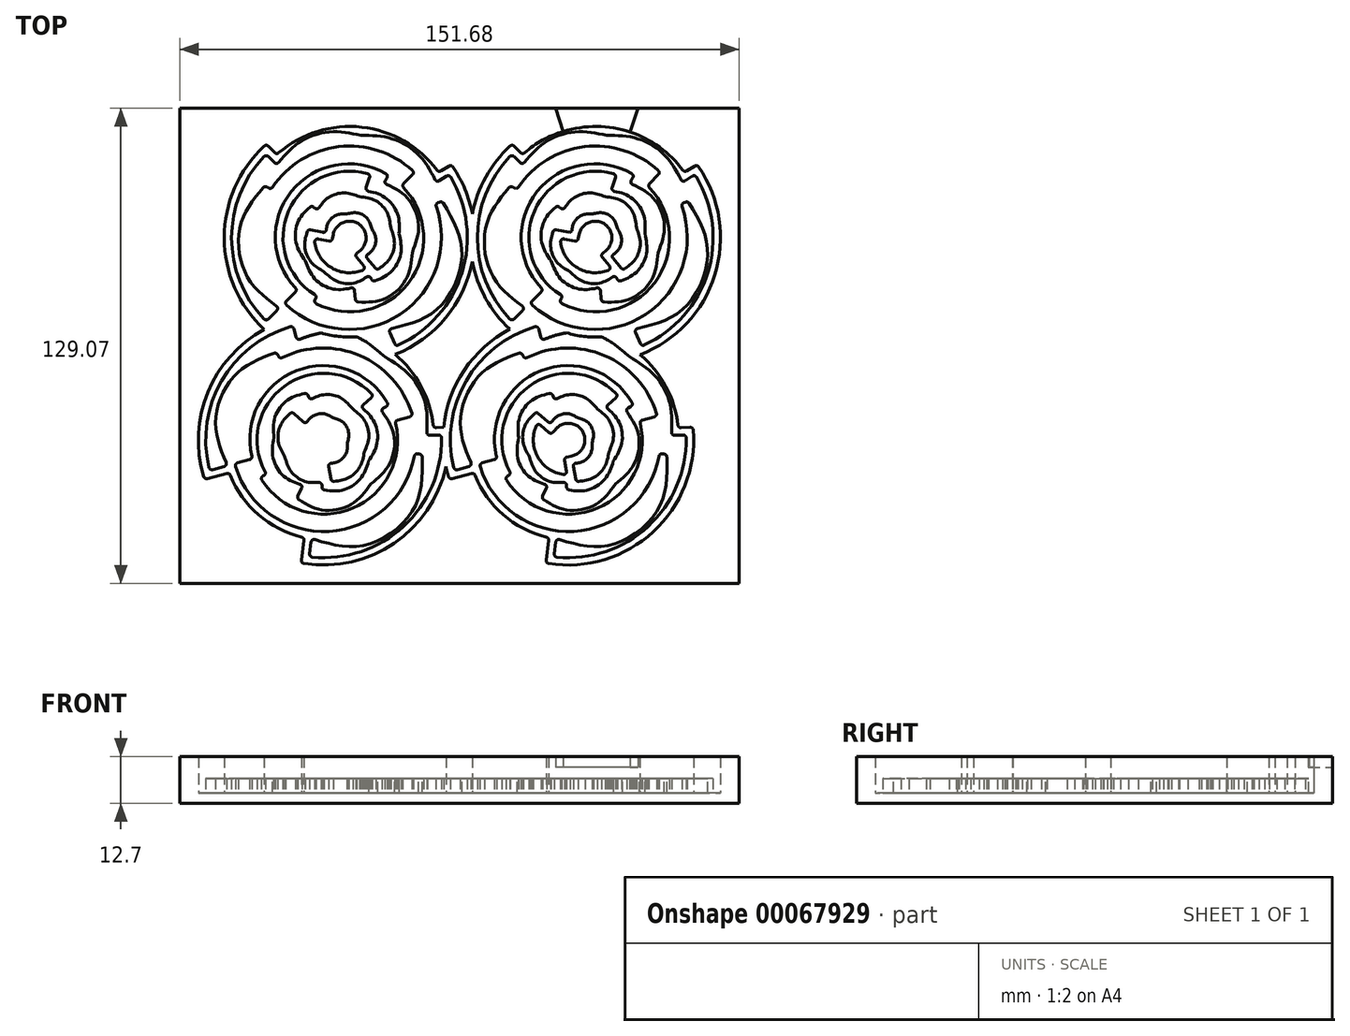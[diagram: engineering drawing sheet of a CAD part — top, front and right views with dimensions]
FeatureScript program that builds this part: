
annotation { "Feature Type Name" : "Feature", "Feature Type Description" : "" }
export const myFeature = defineFeature(function(context is Context, id is Id, definition is map)
    precondition{}
    {
        {
            var Q0;
            Q0=qCreatedBy(makeId("Front.planeOp"),FACE);
            var sketch = newSketch(context, id + "F0", { "sketchPlane" : qUnion([Q0])});
            skCircle(sketch, "E0", {"center": v(0, -1.15) * mm, "radius": 34.66 * mm});
            skSolve(sketch);
        }
        {
            var Q0;
            Q0 = qSketchRegion(id + "F0", true);
            extrude(context, id + "F1", {"entities" : qUnion([Q0]), "depth" : 4 * mm});
        }
        {
            var Q0;
            Q0=qCreatedBy(makeId("Front.planeOp"),FACE);
            var sketch = newSketch(context, id + "F2", { "sketchPlane" : qUnion([Q0])});
            skLineSegment(sketch, "E1", {"start": v(14.14, -15.15) * mm, "end": v(17.68, -18.69) * mm});
            skLineSegment(sketch, "E2", {"start": v(-21.29, -14.11) * mm, "end": v(-23, -15.16) * mm});
            skFitSpline(sketch, "E3", {"points": [v(-23, -15.16) * mm, v(-29.55, -4.51) * mm, v(-27.93, 9.24) * mm, v(-19.1, 18.08) * mm]});
            skLineSegment(sketch, "E4", {"start": v(-19.1, 18.08) * mm, "end": v(-22.63, 21.62) * mm});
            skLineSegment(sketch, "E5", {"start": v(-22.63, -23.64) * mm, "end": v(-19.8, -20.8) * mm});
            skFitSpline(sketch, "E6", {"points": [v(3.07, -28.84) * mm, v(-5.38, -29.77) * mm, v(-13.8, -26.82) * mm, v(-19.8, -20.8) * mm]});
            skFitSpline(sketch, "E7", {"points": [v(23.63, -16.03) * mm, v(19.08, -23.2) * mm, v(11.51, -27.91) * mm, v(3.07, -28.84) * mm]});
            skLineSegment(sketch, "E8", {"start": v(23.63, -16.03) * mm, "end": v(27.01, -18.17) * mm});
            skLineSegment(sketch, "E9", {"start": v(12.52, 28.44) * mm, "end": v(10.56, 23.84) * mm});
            skFitSpline(sketch, "E10", {"points": [v(10.56, 23.84) * mm, v(24.04, 18.11) * mm, v(30.5, 2.69) * mm, v(25.11, -10.93) * mm]});
            skLineSegment(sketch, "E11", {"start": v(25.11, -10.93) * mm, "end": v(23.25, -10.2) * mm});
            skLineSegment(sketch, "E12", {"start": v(-17.68, 16.67) * mm, "end": v(-14.14, 13.13) * mm});
            skLineSegment(sketch, "E13", {"start": v(10.59, -17.98) * mm, "end": v(9.26, -15.86) * mm});
            skFitSpline(sketch, "E14", {"points": [v(17.04, 3) * mm, v(18.75, -4.3) * mm, v(15.63, -11.89) * mm, v(9.26, -15.86) * mm]});
            skFitSpline(sketch, "E15", {"points": [v(1.68, 16.4) * mm, v(9.15, 15.69) * mm, v(15.32, 10.3) * mm, v(17.04, 3) * mm]});
            skLineSegment(sketch, "E16", {"start": v(1.68, 16.4) * mm, "end": v(1.3, 12.43) * mm});
            skFitSpline(sketch, "E17", {"points": [v(-11.98, 5.22) * mm, v(-9.44, 10.1) * mm, v(-4.18, 12.96) * mm, v(1.3, 12.43) * mm]});
            skFitSpline(sketch, "E18", {"points": [v(-10.25, -9.79) * mm, v(-13.84, -5.6) * mm, v(-14.52, 0.33) * mm, v(-11.98, 5.22) * mm]});
            skLineSegment(sketch, "E19", {"start": v(-10.25, -9.79) * mm, "end": v(-8.74, -8.49) * mm});
            skFitSpline(sketch, "E20", {"points": [v(2.7, -12.19) * mm, v(-1.5, -13.2) * mm, v(-5.92, -11.77) * mm, v(-8.74, -8.49) * mm]});
            skFitSpline(sketch, "E21", {"points": [v(11.19, -3.69) * mm, v(10.18, -7.9) * mm, v(6.9, -11.18) * mm, v(2.7, -12.19) * mm]});
            skFitSpline(sketch, "E22", {"points": [v(7.46, 7.74) * mm, v(10.75, 4.93) * mm, v(12.2, 0.52) * mm, v(11.19, -3.69) * mm]});
            skLineSegment(sketch, "E23", {"start": v(7.46, 7.74) * mm, "end": v(4.22, 3.94) * mm});
            skFitSpline(sketch, "E24", {"points": [v(-0.66, -7.48) * mm, v(-3.5, -7.19) * mm, v(-5.8, -5.1) * mm, v(-6.37, -2.3) * mm]});
            skFitSpline(sketch, "E25", {"points": [v(5.98, -3.57) * mm, v(4.86, -6.18) * mm, v(2.17, -7.77) * mm, v(-0.66, -7.48) * mm]});
            skFitSpline(sketch, "E26", {"points": [v(4.22, 3.94) * mm, v(6.38, 2.09) * mm, v(7.1, -0.95) * mm, v(5.98, -3.57) * mm]});
            skLineSegment(sketch, "E27", {"start": v(-6.37, -2.3) * mm, "end": v(-11.27, -3.3) * mm});
            skFitSpline(sketch, "E28", {"points": [v(-6.89, 8.2) * mm, v(-3.33, 10.86) * mm, v(1.45, 11.23) * mm, v(5.38, 9.16) * mm]});
            skFitSpline(sketch, "E29", {"points": [v(-11.27, -3.3) * mm, v(-12.15, 1.06) * mm, v(-10.45, 5.54) * mm, v(-6.89, 8.2) * mm]});
            skLineSegment(sketch, "E30", {"start": v(5.38, 9.16) * mm, "end": v(6.31, 10.92) * mm});
            skFitSpline(sketch, "E31", {"points": [v(13.45, -2.13) * mm, v(13, -7.51) * mm, v(9.4, -12.11) * mm, v(4.26, -13.82) * mm]});
            skFitSpline(sketch, "E32", {"points": [v(6.31, 10.92) * mm, v(11.1, 8.4) * mm, v(13.9, 3.26) * mm, v(13.45, -2.13) * mm]});
            skLineSegment(sketch, "E33", {"start": v(4.26, -13.82) * mm, "end": v(5.7, -18.17) * mm});
            skLineSegment(sketch, "E34", {"start": v(-8.81, 14.78) * mm, "end": v(-9.75, 16.45) * mm});
            skArc(sketch, "E35", {"start": v(-22.63, 21.62) * mm, "mid": v(-32, -1) * mm, "end": v(-22.63, -23.64) * mm});
            skArc(sketch, "E36", {"start": v(27.01, -18.17) * mm, "mid": v(30.52, 8.48) * mm, "end": v(12.52, 28.44) * mm});
            skArc(sketch, "E37", {"start": v(23.25, -10.2) * mm, "mid": v(13.66, 19.8) * mm, "end": v(-17.68, 16.67) * mm});
            skArc(sketch, "E38", {"start": v(-21.29, -14.11) * mm, "mid": v(-2.9, -25.73) * mm, "end": v(17.68, -18.69) * mm});
            skArc(sketch, "E39", {"start": v(-14.14, 13.13) * mm, "mid": v(-15.78, -13.55) * mm, "end": v(10.59, -17.98) * mm});
            skArc(sketch, "E40", {"start": v(-8.81, 14.78) * mm, "mid": v(-16.51, -8.29) * mm, "end": v(5.7, -18.17) * mm});
            skArc(sketch, "E41", {"start": v(14.14, -15.15) * mm, "mid": v(16.1, 11.15) * mm, "end": v(-9.75, 16.45) * mm});
            skSolve(sketch);
        }
        {
            var Q0;
            Q0 = qSketchRegion(id + "F2", true);
            extrude(context, id + "F3", {"entities" : qUnion([Q0]), "operationType" : NewBodyOperationType.REMOVE, "endBound" : BoundingType.SYMMETRIC, "oppositeDirection" : true, "depth" : 8 * mm});
        }
        {
            var Q0;
            Q0=makeQuery(id+"F1.opExtrude","CAP_FACE",FACE,{"disambiguationData":[OSD([sQuery(id+"F0.wireOp",EDGE,"E0")])],"isStart":false});
            var sketch = newSketch(context, id + "F4", { "sketchPlane" : qUnion([Q0])});
            skArc(sketch, "E42.1", {"start": v(27.58, -20.9) * mm, "mid": v(32.43, 9.07) * mm, "end": v(11.44, 31.01) * mm});
            skArc(sketch, "E43", {"start": v(8.72, 24.62) * mm, "mid": v(-5.14, 25.45) * mm, "end": v(-17.68, 19.5) * mm});
            skCircle(sketch, "E44", {"center": v(0.17, -1.9) * mm, "radius": 36.8 * mm});
            skLineSegment(sketch, "E45", {"start": v(-17.68, 19.5) * mm, "end": v(-22.58, 24.4) * mm});
            skLineSegment(sketch, "E46", {"start": v(8.72, 24.62) * mm, "end": v(11.44, 31.01) * mm});
            skLineSegment(sketch, "E47", {"start": v(24.2, -18.75) * mm, "end": v(27.58, -20.9) * mm});
            skLineSegment(sketch, "E48", {"start": v(-19.75, -23.6) * mm, "end": v(-22.58, -26.42) * mm});
            skArc(sketch, "E49", {"start": v(-19.75, -23.6) * mm, "mid": v(3.3, -31.05) * mm, "end": v(24.2, -18.75) * mm});
            skArc(sketch, "E50", {"start": v(-22.58, 24.4) * mm, "mid": v(-34, -1) * mm, "end": v(-22.58, -26.42) * mm});
            skSolve(sketch);
        }
        {
            var Q0;
            Q0 = qSketchRegion(id + "F4", true);
            extrude(context, id + "F5", {"entities" : qUnion([Q0]), "operationType" : NewBodyOperationType.REMOVE, "endBound" : BoundingType.SYMMETRIC, "oppositeDirection" : true, "depth" : 25 * mm});
        }
        {
            var Q0;
            Q0=makeQuery(id+"F3.boolean.opBoolean","COPY",EDGE,{"derivedFrom":makeQuery(id+"F3.opExtrude","SWEPT_EDGE",EDGE,{"disambiguationData":[OSD([sQuery(id+"F2.wireOp",EDGE,"E8"),sQuery(id+"F2.wireOp",EDGE,"E36")])]})});
            var Q1;
            Q1=makeQuery(id+"F3.boolean.opBoolean","COPY",EDGE,{"derivedFrom":makeQuery(id+"F3.opExtrude","SWEPT_EDGE",EDGE,{"disambiguationData":[OSD([sQuery(id+"F2.wireOp",EDGE,"E1"),sQuery(id+"F2.wireOp",EDGE,"E41")])]})});
            var Q2;
            Q2=makeQuery(id+"F3.boolean.opBoolean","COPY",EDGE,{"derivedFrom":makeQuery(id+"F3.opExtrude","SWEPT_EDGE",EDGE,{"disambiguationData":[OSD([sQuery(id+"F2.wireOp",EDGE,"E31"),sQuery(id+"F2.wireOp",EDGE,"E33")])]})});
            var Q3;
            Q3=makeQuery(id+"F3.boolean.opBoolean","COPY",EDGE,{"derivedFrom":makeQuery(id+"F3.opExtrude","SWEPT_EDGE",EDGE,{"disambiguationData":[OSD([sQuery(id+"F2.wireOp",EDGE,"E5"),sQuery(id+"F2.wireOp",EDGE,"E35")])]})});
            var Q4;
            Q4=makeQuery(id+"F3.boolean.opBoolean","COPY",EDGE,{"derivedFrom":makeQuery(id+"F3.opExtrude","SWEPT_EDGE",EDGE,{"disambiguationData":[OSD([sQuery(id+"F2.wireOp",EDGE,"E2"),sQuery(id+"F2.wireOp",EDGE,"E38")])]})});
            var Q5;
            Q5=makeQuery(id+"F3.boolean.opBoolean","COPY",EDGE,{"derivedFrom":makeQuery(id+"F3.opExtrude","SWEPT_EDGE",EDGE,{"disambiguationData":[OSD([sQuery(id+"F2.wireOp",EDGE,"E4"),sQuery(id+"F2.wireOp",EDGE,"E35")])]})});
            var Q6;
            Q6=makeQuery(id+"F3.boolean.opBoolean","COPY",EDGE,{"derivedFrom":makeQuery(id+"F3.opExtrude","SWEPT_EDGE",EDGE,{"disambiguationData":[OSD([sQuery(id+"F2.wireOp",EDGE,"E12"),sQuery(id+"F2.wireOp",EDGE,"E37")])]})});
            var Q7;
            Q7=makeQuery(id+"F3.boolean.opBoolean","COPY",EDGE,{"derivedFrom":makeQuery(id+"F3.opExtrude","SWEPT_EDGE",EDGE,{"disambiguationData":[OSD([sQuery(id+"F2.wireOp",EDGE,"E34"),sQuery(id+"F2.wireOp",EDGE,"E40")])]})});
            var Q8;
            Q8=makeQuery(id+"F3.boolean.opBoolean","COPY",EDGE,{"derivedFrom":makeQuery(id+"F3.opExtrude","SWEPT_EDGE",EDGE,{"disambiguationData":[OSD([sQuery(id+"F2.wireOp",EDGE,"E28"),sQuery(id+"F2.wireOp",EDGE,"E30")])]})});
            var Q9;
            Q9=makeQuery(id+"F3.boolean.opBoolean","COPY",EDGE,{"derivedFrom":makeQuery(id+"F3.opExtrude","SWEPT_EDGE",EDGE,{"disambiguationData":[OSD([sQuery(id+"F2.wireOp",EDGE,"E18"),sQuery(id+"F2.wireOp",EDGE,"E19")])]})});
            var Q10;
            Q10=makeQuery(id+"F3.boolean.opBoolean","COPY",EDGE,{"derivedFrom":makeQuery(id+"F3.opExtrude","SWEPT_EDGE",EDGE,{"disambiguationData":[OSD([sQuery(id+"F2.wireOp",EDGE,"E24"),sQuery(id+"F2.wireOp",EDGE,"E27")])]})});
            var Q11;
            Q11=makeQuery(id+"F3.boolean.opBoolean","COPY",EDGE,{"derivedFrom":makeQuery(id+"F3.opExtrude","SWEPT_EDGE",EDGE,{"disambiguationData":[OSD([sQuery(id+"F2.wireOp",EDGE,"E23"),sQuery(id+"F2.wireOp",EDGE,"E26")])]})});
            var Q12;
            Q12=makeQuery(id+"F3.boolean.opBoolean","COPY",EDGE,{"derivedFrom":makeQuery(id+"F3.opExtrude","SWEPT_EDGE",EDGE,{"disambiguationData":[OSD([sQuery(id+"F2.wireOp",EDGE,"E9"),sQuery(id+"F2.wireOp",EDGE,"E10")])]})});
            var Q13;
            Q13=makeQuery(id+"F3.boolean.opBoolean","COPY",EDGE,{"derivedFrom":makeQuery(id+"F3.opExtrude","SWEPT_EDGE",EDGE,{"disambiguationData":[OSD([sQuery(id+"F2.wireOp",EDGE,"E9"),sQuery(id+"F2.wireOp",EDGE,"E36")])]})});
            var Q14;
            Q14=makeQuery(id+"F3.boolean.opBoolean","COPY",EDGE,{"derivedFrom":makeQuery(id+"F3.opExtrude","SWEPT_EDGE",EDGE,{"disambiguationData":[OSD([sQuery(id+"F2.wireOp",EDGE,"E13"),sQuery(id+"F2.wireOp",EDGE,"E39")])]})});
            var Q15;
            Q15=makeQuery(id+"F3.boolean.opBoolean","COPY",EDGE,{"derivedFrom":makeQuery(id+"F3.opExtrude","SWEPT_EDGE",EDGE,{"disambiguationData":[OSD([sQuery(id+"F2.wireOp",EDGE,"E3"),sQuery(id+"F2.wireOp",EDGE,"E4")])]})});
            var Q16;
            Q16=makeQuery(id+"F3.boolean.opBoolean","COPY",EDGE,{"derivedFrom":makeQuery(id+"F3.opExtrude","SWEPT_EDGE",EDGE,{"disambiguationData":[OSD([sQuery(id+"F2.wireOp",EDGE,"E1"),sQuery(id+"F2.wireOp",EDGE,"E38")])]})});
            var Q17;
            Q17=makeQuery(id+"F3.boolean.opBoolean","COPY",EDGE,{"derivedFrom":makeQuery(id+"F3.opExtrude","SWEPT_EDGE",EDGE,{"disambiguationData":[OSD([sQuery(id+"F2.wireOp",EDGE,"E11"),sQuery(id+"F2.wireOp",EDGE,"E37")])]})});
            var Q18;
            Q18=makeQuery(id+"F3.boolean.opBoolean","COPY",EDGE,{"derivedFrom":makeQuery(id+"F3.opExtrude","SWEPT_EDGE",EDGE,{"disambiguationData":[OSD([sQuery(id+"F2.wireOp",EDGE,"E12"),sQuery(id+"F2.wireOp",EDGE,"E39")])]})});
            var Q19;
            Q19=makeQuery(id+"F3.boolean.opBoolean","COPY",EDGE,{"derivedFrom":makeQuery(id+"F3.opExtrude","SWEPT_EDGE",EDGE,{"disambiguationData":[OSD([sQuery(id+"F2.wireOp",EDGE,"E34"),sQuery(id+"F2.wireOp",EDGE,"E41")])]})});
            var Q20;
            Q20=makeQuery(id+"F3.boolean.opBoolean","COPY",EDGE,{"derivedFrom":makeQuery(id+"F3.opExtrude","SWEPT_EDGE",EDGE,{"disambiguationData":[OSD([sQuery(id+"F2.wireOp",EDGE,"E30"),sQuery(id+"F2.wireOp",EDGE,"E32")])]})});
            var Q21;
            Q21=makeQuery(id+"F3.boolean.opBoolean","COPY",EDGE,{"derivedFrom":makeQuery(id+"F3.opExtrude","SWEPT_EDGE",EDGE,{"disambiguationData":[OSD([sQuery(id+"F2.wireOp",EDGE,"E27"),sQuery(id+"F2.wireOp",EDGE,"E29")])]})});
            var Q22;
            Q22=makeQuery(id+"F3.boolean.opBoolean","COPY",EDGE,{"derivedFrom":makeQuery(id+"F3.opExtrude","SWEPT_EDGE",EDGE,{"disambiguationData":[OSD([sQuery(id+"F2.wireOp",EDGE,"E22"),sQuery(id+"F2.wireOp",EDGE,"E23")])]})});
            var Q23;
            Q23=makeQuery(id+"F3.boolean.opBoolean","COPY",EDGE,{"derivedFrom":makeQuery(id+"F3.opExtrude","SWEPT_EDGE",EDGE,{"disambiguationData":[OSD([sQuery(id+"F2.wireOp",EDGE,"E13"),sQuery(id+"F2.wireOp",EDGE,"E14")])]})});
            var Q24;
            Q24=makeQuery(id+"F3.boolean.opBoolean","COPY",EDGE,{"derivedFrom":makeQuery(id+"F3.opExtrude","SWEPT_EDGE",EDGE,{"disambiguationData":[OSD([sQuery(id+"F2.wireOp",EDGE,"E10"),sQuery(id+"F2.wireOp",EDGE,"E11")])]})});
            var Q25;
            Q25=makeQuery(id+"F3.boolean.opBoolean","COPY",EDGE,{"derivedFrom":makeQuery(id+"F3.opExtrude","SWEPT_EDGE",EDGE,{"disambiguationData":[OSD([sQuery(id+"F2.wireOp",EDGE,"E7"),sQuery(id+"F2.wireOp",EDGE,"E8")])]})});
            var Q26;
            Q26=makeQuery(id+"F3.boolean.opBoolean","COPY",EDGE,{"derivedFrom":makeQuery(id+"F3.opExtrude","SWEPT_EDGE",EDGE,{"disambiguationData":[OSD([sQuery(id+"F2.wireOp",EDGE,"E5"),sQuery(id+"F2.wireOp",EDGE,"E6")])]})});
            var Q27;
            Q27=makeQuery(id+"F3.boolean.opBoolean","COPY",EDGE,{"derivedFrom":makeQuery(id+"F3.opExtrude","SWEPT_EDGE",EDGE,{"disambiguationData":[OSD([sQuery(id+"F2.wireOp",EDGE,"E16"),sQuery(id+"F2.wireOp",EDGE,"E17")])]})});
            var Q28;
            Q28=makeQuery(id+"F3.boolean.opBoolean","COPY",EDGE,{"derivedFrom":makeQuery(id+"F3.opExtrude","SWEPT_EDGE",EDGE,{"disambiguationData":[OSD([sQuery(id+"F2.wireOp",EDGE,"E15"),sQuery(id+"F2.wireOp",EDGE,"E16")])]})});
            var Q29;
            Q29=makeQuery(id+"F3.boolean.opBoolean","COPY",EDGE,{"derivedFrom":makeQuery(id+"F3.opExtrude","SWEPT_EDGE",EDGE,{"disambiguationData":[OSD([sQuery(id+"F2.wireOp",EDGE,"E33"),sQuery(id+"F2.wireOp",EDGE,"E40")])]})});
            var Q30;
            Q30=makeQuery(id+"F3.boolean.opBoolean","COPY",EDGE,{"derivedFrom":makeQuery(id+"F3.opExtrude","SWEPT_EDGE",EDGE,{"disambiguationData":[OSD([sQuery(id+"F2.wireOp",EDGE,"E19"),sQuery(id+"F2.wireOp",EDGE,"E20")])]})});
            var Q31;
            Q31=makeQuery(id+"F5.boolean.opBoolean","COPY",EDGE,{"derivedFrom":makeQuery(id+"F5.opExtrude","SWEPT_EDGE",EDGE,{"disambiguationData":[OSD([sQuery(id+"F4.wireOp",EDGE,"E43"),sQuery(id+"F4.wireOp",EDGE,"E46")])]})});
            var Q32;
            Q32=makeQuery(id+"F5.boolean.opBoolean","COPY",EDGE,{"derivedFrom":makeQuery(id+"F5.opExtrude","SWEPT_EDGE",EDGE,{"disambiguationData":[OSD([sQuery(id+"F4.wireOp",EDGE,"E43"),sQuery(id+"F4.wireOp",EDGE,"E45")])]})});
            var Q33;
            Q33=makeQuery(id+"F5.boolean.opBoolean","COPY",EDGE,{"derivedFrom":makeQuery(id+"F5.opExtrude","SWEPT_EDGE",EDGE,{"disambiguationData":[OSD([sQuery(id+"F4.wireOp",EDGE,"E45"),sQuery(id+"F4.wireOp",EDGE,"E50")])]})});
            var Q34;
            Q34=makeQuery(id+"F5.boolean.opBoolean","COPY",EDGE,{"derivedFrom":makeQuery(id+"F5.opExtrude","SWEPT_EDGE",EDGE,{"disambiguationData":[OSD([sQuery(id+"F4.wireOp",EDGE,"E42.1"),sQuery(id+"F4.wireOp",EDGE,"E46")])]})});
            var Q35;
            Q35=makeQuery(id+"F5.boolean.opBoolean","COPY",EDGE,{"derivedFrom":makeQuery(id+"F5.opExtrude","SWEPT_EDGE",EDGE,{"disambiguationData":[OSD([sQuery(id+"F4.wireOp",EDGE,"E48"),sQuery(id+"F4.wireOp",EDGE,"E49")])]})});
            var Q36;
            Q36=makeQuery(id+"F5.boolean.opBoolean","COPY",EDGE,{"derivedFrom":makeQuery(id+"F5.opExtrude","SWEPT_EDGE",EDGE,{"disambiguationData":[OSD([sQuery(id+"F4.wireOp",EDGE,"E48"),sQuery(id+"F4.wireOp",EDGE,"E50")])]})});
            var Q37;
            Q37=makeQuery(id+"F5.boolean.opBoolean","COPY",EDGE,{"derivedFrom":makeQuery(id+"F5.opExtrude","SWEPT_EDGE",EDGE,{"disambiguationData":[OSD([sQuery(id+"F4.wireOp",EDGE,"E47"),sQuery(id+"F4.wireOp",EDGE,"E49")])]})});
            var Q38;
            Q38=makeQuery(id+"F5.boolean.opBoolean","COPY",EDGE,{"derivedFrom":makeQuery(id+"F5.opExtrude","SWEPT_EDGE",EDGE,{"disambiguationData":[OSD([sQuery(id+"F4.wireOp",EDGE,"E42.1"),sQuery(id+"F4.wireOp",EDGE,"E47")])]})});
            var Q39;
            Q39=makeQuery(id+"F3.boolean.opBoolean","COPY",EDGE,{"derivedFrom":makeQuery(id+"F3.opExtrude","SWEPT_EDGE",EDGE,{"disambiguationData":[OSD([sQuery(id+"F2.wireOp",EDGE,"E2"),sQuery(id+"F2.wireOp",EDGE,"E3")])]})});
            fillet(context, id + "F6", {"entities" : qUnion([Q0, Q1, Q2, Q3, Q4, Q5, Q6, Q7, Q8, Q9, Q10, Q11, Q12, Q13, Q14, Q15, Q16, Q17, Q18, Q19, Q20, Q21, Q22, Q23, Q24, Q25, Q26, Q27, Q28, Q29, Q30, Q31, Q32, Q33, Q34, Q35, Q36, Q37, Q38, Q39]), "radius" : .8 * mm, "tangentPropagation" : true, "allowEdgeOverflow" : false});
        }
        {
            var Q0;
            Q0=makeQuery(id+"F1.opExtrude","CAP_FACE",FACE,{"disambiguationData":[OSD([sQuery(id+"F0.wireOp",EDGE,"E0")])],"isStart":false});
            var sketch = newSketch(context, id + "F7", { "sketchPlane" : qUnion([Q0])});
            skLineSegment(sketch, "E51.0", {"start": v(-19.06, 15.24) * mm, "end": v(-16.88, 13.07) * mm});
            skArc(sketch, "E52.0", {"start": v(-15.5, 14.55) * mm, "mid": v(-15.51, 14.54) * mm, "end": v(-15.52, 14.53) * mm});
            skArc(sketch, "E53.trimOffspring", {"start": v(-16.88, 13.07) * mm, "mid": v(-16.15, -16.16) * mm, "end": v(12.97, -18.8) * mm});
            skFitSpline(sketch, "E54.0", {"points": [v(-21.25, -14.13) * mm, v(-22.77, -11.66) * mm, v(-24.86, -6.37) * mm, v(-25.24, 1.94) * mm, v(-22.94, 9.95) * mm, v(-19.69, 14.6) * mm, v(-17.64, 16.66) * mm]});
            skLineSegment(sketch, "E54.1", {"start": v(-20.54, -11.34) * mm, "end": v(-22.23, -12.38) * mm});
            skArc(sketch, "E54.2", {"start": v(-20.54, -11.34) * mm, "mid": v(-4.6, -23.44) * mm, "end": v(14.81, -18.63) * mm});
            skLineSegment(sketch, "E54.3", {"start": v(12.76, -16.58) * mm, "end": v(14.81, -18.63) * mm});
            skFitSpline(sketch, "E55.trimOffspring", {"points": [v(-21.25, -14.13) * mm, v(-22.77, -11.66) * mm, v(-24.86, -6.37) * mm, v(-25.24, 1.94) * mm, v(-22.94, 9.95) * mm, v(-19.69, 14.6) * mm, v(-17.64, 16.66) * mm, v(-21.25, -14.13) * mm]});
            skLineSegment(sketch, "E56", {"start": v(12.76, -16.58) * mm, "end": v(11.86, -17.22) * mm});
            skLineSegment(sketch, "E57", {"start": v(11.86, -17.22) * mm, "end": v(12.97, -18.8) * mm});
            skLineSegment(sketch, "E58", {"start": v(4.57, 7.42) * mm, "end": v(4.62, 7.48) * mm});
            skLineSegment(sketch, "E59.2", {"start": v(-5.74, 13.39) * mm, "end": v(-6.98, 15.6) * mm});
            skArc(sketch, "E59.3", {"start": v(-0.26, 17.08) * mm, "mid": v(-3.7, 16.67) * mm, "end": v(-6.98, 15.6) * mm});
            skFitSpline(sketch, "E60.1", {"points": [v(-13.75, 6.14) * mm, v(-13.02, 7.54) * mm, v(-11.17, 10.06) * mm, v(-7.5, 12.8) * mm, v(-3.2, 14.39) * mm, v(-0.08, 14.57) * mm, v(1.5, 14.42) * mm]});
            skArc(sketch, "E61", {"start": v(-8.84, -11.21) * mm, "mid": v(-3.6, -13.99) * mm, "end": v(2.32, -14.3) * mm});
            skLineSegment(sketch, "E62", {"start": v(-10.8, -12.89) * mm, "end": v(-8.84, -11.21) * mm});
            skLineSegment(sketch, "E63", {"start": v(3.14, -16.78) * mm, "end": v(2.32, -14.3) * mm});
            skArc(sketch, "E64", {"start": v(-10.8, -12.89) * mm, "mid": v(-4.3, -16.51) * mm, "end": v(3.14, -16.78) * mm});
            skLineSegment(sketch, "E65", {"start": v(-0.51, 14.48) * mm, "end": v(-0.26, 17.08) * mm});
            skLineSegment(sketch, "E66.0", {"start": v(-4.5, -1.92) * mm, "end": v(-4.96, 0.36) * mm});
            skLineSegment(sketch, "E66.1", {"start": v(2.99, 2.48) * mm, "end": v(1.1, 4.07) * mm});
            skFitSpline(sketch, "E66.2", {"points": [v(2.99, 2.48) * mm, v(3.37, 2.16) * mm, v(4, 1.4) * mm, v(4.55, 0.05) * mm, v(4.66, -1.4) * mm, v(4.42, -2.36) * mm, v(4.22, -2.82) * mm]});
            skFitSpline(sketch, "E66.3", {"points": [v(4.22, -2.81) * mm, v(4.03, -3.28) * mm, v(3.5, -4.1) * mm, v(2.37, -5.03) * mm, v(1.02, -5.57) * mm, v(0.04, -5.63) * mm, v(-0.47, -5.58) * mm]});
            skFitSpline(sketch, "E66.4", {"points": [v(-0.47, -5.58) * mm, v(-0.97, -5.53) * mm, v(-1.92, -5.27) * mm, v(-3.13, -4.47) * mm, v(-4.05, -3.34) * mm, v(-4.4, -2.42) * mm, v(-4.5, -1.92) * mm]});
            skLineSegment(sketch, "E67.1", {"start": v(-5.45, 0.26) * mm, "end": v(-8.74, -0.4) * mm});
            skLineSegment(sketch, "E68.0", {"start": v(1.42, 4.46) * mm, "end": v(3.78, 7.26) * mm});
            skArc(sketch, "E69.trimOffspring", {"start": v(3.78, 7.26) * mm, "mid": v(-4.53, 6.78) * mm, "end": v(-8.74, -0.4) * mm});
            skLineSegment(sketch, "E70", {"start": v(1.42, 4.46) * mm, "end": v(1.1, 4.07) * mm});
            skLineSegment(sketch, "E71", {"start": v(-5.45, 0.26) * mm, "end": v(-4.96, 0.36) * mm});
            skSolve(sketch);
        }
        {
            var Q0;
            Q0=makeQuery(id+"F1.opExtrude","CAP_FACE",FACE,{"disambiguationData":[OSD([sQuery(id+"F0.wireOp",EDGE,"E0")])],"isStart":true});
            var sketch = newSketch(context, id + "F8", { "sketchPlane" : qUnion([Q0])});
            skArc(sketch, "E72.0", {"start": v(-28.03, -20.27) * mm, "mid": v(-32.43, 9.07) * mm, "end": v(-12.16, 30.74) * mm});
            skLineSegment(sketch, "E73.0", {"start": v(-9, 25.29) * mm, "end": v(-11.14, 30.31) * mm});
            skArc(sketch, "E74.0", {"start": v(-8.04, 24.83) * mm, "mid": v(5.14, 25.45) * mm, "end": v(17.12, 19.94) * mm});
            skLineSegment(sketch, "E75.0", {"start": v(18.19, 20) * mm, "end": v(22.04, 23.86) * mm});
            skArc(sketch, "E76.0", {"start": v(23.16, 23.88) * mm, "mid": v(34, -1) * mm, "end": v(23.16, -25.9) * mm});
            skArc(sketch, "E77.0", {"start": v(19.2, -24.08) * mm, "mid": v(-3.3, -31.05) * mm, "end": v(-23.76, -19.35) * mm});
            skLineSegment(sketch, "E78.0", {"start": v(20.28, -24.12) * mm, "end": v(22.04, -25.88) * mm});
            skLineSegment(sketch, "E79.0", {"start": v(-24.83, -19.15) * mm, "end": v(-26.94, -20.5) * mm});
            skArc(sketch, "E80.0", {"start": v(-11.14, 30.31) * mm, "mid": v(-11.56, 30.73) * mm, "end": v(-12.16, 30.74) * mm});
            skArc(sketch, "E81.0", {"start": v(-8.04, 24.83) * mm, "mid": v(-8.6, 24.88) * mm, "end": v(-9, 25.29) * mm});
            skArc(sketch, "E82.0", {"start": v(18.19, 20) * mm, "mid": v(17.67, 19.77) * mm, "end": v(17.12, 19.94) * mm});
            skArc(sketch, "E83.0", {"start": v(23.16, 23.88) * mm, "mid": v(22.6, 24.1) * mm, "end": v(22.04, 23.86) * mm});
            skArc(sketch, "E84.0", {"start": v(22.04, -25.88) * mm, "mid": v(22.6, -26.12) * mm, "end": v(23.16, -25.9) * mm});
            skArc(sketch, "E85.0", {"start": v(19.2, -24.08) * mm, "mid": v(19.75, -23.89) * mm, "end": v(20.28, -24.12) * mm});
            skArc(sketch, "E86.0", {"start": v(-24.83, -19.15) * mm, "mid": v(-24.25, -19.04) * mm, "end": v(-23.76, -19.35) * mm});
            skArc(sketch, "E87.0", {"start": v(-28.03, -20.27) * mm, "mid": v(-27.53, -20.6) * mm, "end": v(-26.94, -20.5) * mm});
            skSolve(sketch);
        }
        {
            var Q0;
            Q0 = qSketchRegion(id + "F8", true);
            extrude(context, id + "F9", {"entities" : qUnion([Q0]), "operationType" : NewBodyOperationType.ADD, "depth" : .9 * mm});
        }
        {
            var Q0;
            Q0=makeQuery(id+"F1.opExtrude","SWEPT_BODY",BODY,{"disambiguationData":[OSD([sQuery(id+"F0.wireOp",EDGE,"E0")])]});
            transform(context, id + "F10", {"entities" : qUnion([Q0]), "transformType" : TransformType.TRANSLATION_3D, "dx" : 66.7 * mm, "dy" : 0 * mm, "dz" : 0 * mm, "makeCopy" : true});
        }
        {
            var Q0;
            Q0=makeQuery(id+"F1.opExtrude","SWEPT_BODY",BODY,{"disambiguationData":[OSD([sQuery(id+"F0.wireOp",EDGE,"E0")])]});
            transform(context, id + "F11", {"entities" : qUnion([Q0]), "transformType" : TransformType.TRANSLATION_3D, "dx" : 0 * mm, "dy" : 0 * mm, "dz" : 60.7 * mm, "makeCopy" : true});
        }
        {
            var Q0;
            Q0=makeQuery(id+"F11.opPattern","COPY",BODY,{"derivedFrom":makeQuery(id+"F1.opExtrude","SWEPT_BODY",BODY,{"disambiguationData":[OSD([sQuery(id+"F0.wireOp",EDGE,"E0")])]}),"instanceName":"1"});
            var Q1;
            Q1=makeQuery(id+"F11.opPattern","COPY",EDGE,{"derivedFrom":makeQuery(id+"F3.boolean.opBoolean","COPY",EDGE,{"derivedFrom":makeQuery(id+"F3.opExtrude","SWEPT_EDGE",EDGE,{"disambiguationData":[OSD([sQuery(id+"F2.wireOp",EDGE,"E24"),sQuery(id+"F2.wireOp",EDGE,"E25")])]})}),"instanceName":"1"});
            transform(context, id + "F12", {"entities" : qUnion([Q0]), "transformType" : TransformType.ROTATION, "transformAxis" : qUnion([Q1]), "angle" : 30 * degree, "makeCopy" : false});
        }
        {
            var Q0;
            Q0=makeQuery(id+"F11.opPattern","COPY",BODY,{"derivedFrom":makeQuery(id+"F1.opExtrude","SWEPT_BODY",BODY,{"disambiguationData":[OSD([sQuery(id+"F0.wireOp",EDGE,"E0")])]}),"instanceName":"1"});
            transform(context, id + "F13", {"entities" : qUnion([Q0]), "transformType" : TransformType.TRANSLATION_3D, "dx" : -3.7 * mm, "dy" : 0 * mm, "dz" : -5.3 * mm, "makeCopy" : false});
        }
        {
            var Q0;
            Q0=makeQuery(id+"F11.opPattern","COPY",BODY,{"derivedFrom":makeQuery(id+"F1.opExtrude","SWEPT_BODY",BODY,{"disambiguationData":[OSD([sQuery(id+"F0.wireOp",EDGE,"E0")])]}),"instanceName":"1"});
            transform(context, id + "F14", {"entities" : qUnion([Q0]), "transformType" : TransformType.TRANSLATION_3D, "dx" : 66.4 * mm, "dy" : 0 * mm, "dz" : 0 * mm, "makeCopy" : true});
        }
        {
            var Q0;
            Q0=makeQuery(id+"F14.opPattern","COPY",BODY,{"derivedFrom":makeQuery(id+"F11.opPattern","COPY",BODY,{"derivedFrom":makeQuery(id+"F1.opExtrude","SWEPT_BODY",BODY,{"disambiguationData":[OSD([sQuery(id+"F0.wireOp",EDGE,"E0")])]}),"instanceName":"1"}),"instanceName":"1"});
            var Q1;
            Q1=makeQuery(id+"F11.opPattern","COPY",BODY,{"derivedFrom":makeQuery(id+"F1.opExtrude","SWEPT_BODY",BODY,{"disambiguationData":[OSD([sQuery(id+"F0.wireOp",EDGE,"E0")])]}),"instanceName":"1"});
            var Q2;
            Q2=makeQuery(id+"F10.opPattern","COPY",BODY,{"derivedFrom":makeQuery(id+"F1.opExtrude","SWEPT_BODY",BODY,{"disambiguationData":[OSD([sQuery(id+"F0.wireOp",EDGE,"E0")])]}),"instanceName":"1"});
            var Q3;
            Q3=makeQuery(id+"F1.opExtrude","SWEPT_BODY",BODY,{"disambiguationData":[OSD([sQuery(id+"F0.wireOp",EDGE,"E0")])]});
            booleanBodies(context, id + "F15", {"operationType" : BooleanOperationType.UNION, "tools" : qUnion([Q0, Q1, Q2, Q3])});
        }
        {
            var Q0;
            {var subQ0=makeQuery(id+"F1.opExtrude","CAP_FACE",FACE,{"disambiguationData":[OSD([sQuery(id+"F0.wireOp",EDGE,"E0")])],"isStart":false});var subQ1=makeQuery(id+"F11.opPattern","COPY",FACE,{"derivedFrom":subQ0,"instanceName":"1"});Q0=makeQuery(id+"F15.opBoolean","MERGE",FACE,{"derivedFrom":[subQ0,makeQuery(id+"F10.opPattern","COPY",FACE,{"derivedFrom":subQ0,"instanceName":"1"}),subQ1,makeQuery(id+"F14.opPattern","COPY",FACE,{"derivedFrom":subQ1,"instanceName":"1"})]});}
            var sketch = newSketch(context, id + "F16", { "sketchPlane" : qUnion([Q0])});
            skLineSegment(sketch, "E88.0", {"start": v(75.7, 25.29) * mm, "end": v(77.6, 29.74) * mm});
            skArc(sketch, "E89.0", {"start": v(70.4, 25.74) * mm, "mid": v(74.14, 27.49) * mm, "end": v(77.6, 29.74) * mm});
            skArc(sketch, "E90.0", {"start": v(74.74, 24.83) * mm, "mid": v(72.59, 25.37) * mm, "end": v(70.4, 25.74) * mm});
            skArc(sketch, "E91.0", {"start": v(74.74, 24.83) * mm, "mid": v(75.3, 24.88) * mm, "end": v(75.7, 25.29) * mm});
            skArc(sketch, "E92.0", {"start": v(54.3, 24.28) * mm, "mid": v(55.38, 24.1) * mm, "end": v(56.47, 23.95) * mm});
            skArc(sketch, "E93.0", {"start": v(56.47, 23.95) * mm, "mid": v(54.7, 23.16) * mm, "end": v(52.98, 22.25) * mm});
            skLineSegment(sketch, "E94.0", {"start": v(53.37, 23.7) * mm, "end": v(52.98, 22.25) * mm});
            skArc(sketch, "E95.0", {"start": v(54.3, 24.28) * mm, "mid": v(53.72, 24.17) * mm, "end": v(53.37, 23.7) * mm});
            skArc(sketch, "E96.0", {"start": v(50.9, 20.93) * mm, "mid": v(50.23, 20.45) * mm, "end": v(49.58, 19.94) * mm});
            skArc(sketch, "E97.0", {"start": v(45.86, 22.66) * mm, "mid": v(48.34, 21.7) * mm, "end": v(50.9, 20.93) * mm});
            skLineSegment(sketch, "E98.0", {"start": v(48.51, 20) * mm, "end": v(45.86, 22.66) * mm});
            skArc(sketch, "E99.0", {"start": v(48.51, 20) * mm, "mid": v(49.03, 19.77) * mm, "end": v(49.58, 19.94) * mm});
            skArc(sketch, "E100.0", {"start": v(8.04, 24.83) * mm, "mid": v(6, 25.35) * mm, "end": v(3.92, 25.71) * mm});
            skArc(sketch, "E101.0", {"start": v(3.92, 25.71) * mm, "mid": v(7.46, 27.34) * mm, "end": v(10.76, 29.42) * mm});
            skLineSegment(sketch, "E102.0", {"start": v(9, 25.29) * mm, "end": v(10.76, 29.42) * mm});
            skArc(sketch, "E103.0", {"start": v(8.04, 24.83) * mm, "mid": v(8.6, 24.88) * mm, "end": v(9, 25.29) * mm});
            skArc(sketch, "E104.0", {"start": v(-12.1, 24.28) * mm, "mid": v(-11.14, 24.11) * mm, "end": v(-10.16, 23.98) * mm});
            skPoint(sketch, "E105.0", {"position": v(-11.79, 23.27) * mm});
            skArc(sketch, "E106.0", {"start": v(-10.16, 23.98) * mm, "mid": v(-11.79, 23.27) * mm, "end": v(-13.36, 22.45) * mm});
            skLineSegment(sketch, "E107.0", {"start": v(-13.03, 23.7) * mm, "end": v(-13.36, 22.45) * mm});
            skArc(sketch, "E108.0", {"start": v(-12.1, 24.28) * mm, "mid": v(-12.68, 24.17) * mm, "end": v(-13.03, 23.7) * mm});
            skArc(sketch, "E109.0", {"start": v(-15.72, 20.99) * mm, "mid": v(-16.43, 20.48) * mm, "end": v(-17.12, 19.94) * mm});
            skArc(sketch, "E110.0", {"start": v(-21.08, 22.9) * mm, "mid": v(-18.44, 21.83) * mm, "end": v(-15.72, 20.99) * mm});
            skLineSegment(sketch, "E111.0", {"start": v(-18.19, 20) * mm, "end": v(-21.08, 22.9) * mm});
            skArc(sketch, "E112.0", {"start": v(-18.19, 20) * mm, "mid": v(-17.67, 19.77) * mm, "end": v(-17.12, 19.94) * mm});
            skSolve(sketch);
        }
        {
            var Q0;
            Q0 = qSketchRegion(id + "F16", true);
            var Q1;
            {var subQ0=makeQuery(id+"F9.opExtrude","CAP_FACE",FACE,{"disambiguationData":[OSD([sQuery(id+"F8.wireOp",EDGE,"E72.0"),sQuery(id+"F8.wireOp",EDGE,"E73.0"),sQuery(id+"F8.wireOp",EDGE,"E74.0"),sQuery(id+"F8.wireOp",EDGE,"E75.0"),sQuery(id+"F8.wireOp",EDGE,"E76.0"),sQuery(id+"F8.wireOp",EDGE,"E77.0"),sQuery(id+"F8.wireOp",EDGE,"E78.0"),sQuery(id+"F8.wireOp",EDGE,"E79.0"),sQuery(id+"F8.wireOp",EDGE,"E80.0"),sQuery(id+"F8.wireOp",EDGE,"E81.0"),sQuery(id+"F8.wireOp",EDGE,"E82.0"),sQuery(id+"F8.wireOp",EDGE,"E83.0"),sQuery(id+"F8.wireOp",EDGE,"E84.0"),sQuery(id+"F8.wireOp",EDGE,"E85.0"),sQuery(id+"F8.wireOp",EDGE,"E86.0"),sQuery(id+"F8.wireOp",EDGE,"E87.0")])],"isStart":false});var subQ1=makeQuery(id+"F11.opPattern","COPY",FACE,{"derivedFrom":subQ0,"instanceName":"1"});Q1=makeQuery(id+"F15.opBoolean","MERGE",FACE,{"derivedFrom":[subQ0,makeQuery(id+"F10.opPattern","COPY",FACE,{"derivedFrom":subQ0,"instanceName":"1"}),subQ1,makeQuery(id+"F14.opPattern","COPY",FACE,{"derivedFrom":subQ1,"instanceName":"1"})]});}
            extrude(context, id + "F17", {"entities" : qUnion([Q0]), "operationType" : NewBodyOperationType.ADD, "endBound" : BoundingType.UP_TO_SURFACE, "oppositeDirection" : true, "endBoundEntityFace" : qUnion([Q1]), "depth" : 25 * mm});
        }
        {
            var Q0;
            {var subQ0=makeQuery(id+"F9.opExtrude","CAP_FACE",FACE,{"disambiguationData":[OSD([sQuery(id+"F8.wireOp",EDGE,"E72.0"),sQuery(id+"F8.wireOp",EDGE,"E73.0"),sQuery(id+"F8.wireOp",EDGE,"E74.0"),sQuery(id+"F8.wireOp",EDGE,"E75.0"),sQuery(id+"F8.wireOp",EDGE,"E76.0"),sQuery(id+"F8.wireOp",EDGE,"E77.0"),sQuery(id+"F8.wireOp",EDGE,"E78.0"),sQuery(id+"F8.wireOp",EDGE,"E79.0"),sQuery(id+"F8.wireOp",EDGE,"E80.0"),sQuery(id+"F8.wireOp",EDGE,"E81.0"),sQuery(id+"F8.wireOp",EDGE,"E82.0"),sQuery(id+"F8.wireOp",EDGE,"E83.0"),sQuery(id+"F8.wireOp",EDGE,"E84.0"),sQuery(id+"F8.wireOp",EDGE,"E85.0"),sQuery(id+"F8.wireOp",EDGE,"E86.0"),sQuery(id+"F8.wireOp",EDGE,"E87.0")])],"isStart":false});var subQ1=makeQuery(id+"F11.opPattern","COPY",FACE,{"derivedFrom":subQ0,"instanceName":"1"});Q0=makeQuery(id+"F17.boolean.opBoolean","MERGE",FACE,{"derivedFrom":[makeQuery(id+"F15.opBoolean","MERGE",FACE,{"derivedFrom":[subQ0,makeQuery(id+"F10.opPattern","COPY",FACE,{"derivedFrom":subQ0,"instanceName":"1"}),subQ1,makeQuery(id+"F14.opPattern","COPY",FACE,{"derivedFrom":subQ1,"instanceName":"1"})]}),makeQuery(id+"F17.opExtrude","CAP_FACE",FACE,{"disambiguationData":[OSD([sQuery(id+"F16.wireOp",EDGE,"E88.0"),sQuery(id+"F16.wireOp",EDGE,"E89.0"),sQuery(id+"F16.wireOp",EDGE,"E90.0"),sQuery(id+"F16.wireOp",EDGE,"E91.0")])],"isStart":false}),makeQuery(id+"F17.opExtrude","CAP_FACE",FACE,{"disambiguationData":[OSD([sQuery(id+"F16.wireOp",EDGE,"E92.0"),sQuery(id+"F16.wireOp",EDGE,"E93.0"),sQuery(id+"F16.wireOp",EDGE,"E94.0"),sQuery(id+"F16.wireOp",EDGE,"E95.0")])],"isStart":false}),makeQuery(id+"F17.opExtrude","CAP_FACE",FACE,{"disambiguationData":[OSD([sQuery(id+"F16.wireOp",EDGE,"E96.0"),sQuery(id+"F16.wireOp",EDGE,"E97.0"),sQuery(id+"F16.wireOp",EDGE,"E98.0"),sQuery(id+"F16.wireOp",EDGE,"E99.0")])],"isStart":false}),makeQuery(id+"F17.opExtrude","CAP_FACE",FACE,{"disambiguationData":[OSD([sQuery(id+"F16.wireOp",EDGE,"E100.0"),sQuery(id+"F16.wireOp",EDGE,"E101.0"),sQuery(id+"F16.wireOp",EDGE,"E102.0"),sQuery(id+"F16.wireOp",EDGE,"E103.0")])],"isStart":false}),makeQuery(id+"F17.opExtrude","CAP_FACE",FACE,{"disambiguationData":[OSD([sQuery(id+"F16.wireOp",EDGE,"E104.0"),sQuery(id+"F16.wireOp",EDGE,"E106.0"),sQuery(id+"F16.wireOp",EDGE,"E107.0"),sQuery(id+"F16.wireOp",EDGE,"E108.0")])],"isStart":false}),makeQuery(id+"F17.opExtrude","CAP_FACE",FACE,{"disambiguationData":[OSD([sQuery(id+"F16.wireOp",EDGE,"E109.0"),sQuery(id+"F16.wireOp",EDGE,"E110.0"),sQuery(id+"F16.wireOp",EDGE,"E111.0"),sQuery(id+"F16.wireOp",EDGE,"E112.0")])],"isStart":false})]});}
            var sketch = newSketch(context, id + "F18", { "sketchPlane" : qUnion([Q0])});
            skArc(sketch, "E113.0", {"start": v(-33.33, 5.48) * mm, "mid": v(-26.07, 20.76) * mm, "end": v(-12.36, 30.67) * mm});
            skArc(sketch, "E114.0", {"start": v(-25.55, 50.47) * mm, "mid": v(-31.16, 34.9) * mm, "end": v(-43.47, 23.81) * mm});
            skArc(sketch, "E115.0", {"start": v(-43.47, 23.81) * mm, "mid": v(-36.95, 15.45) * mm, "end": v(-33.33, 5.48) * mm});
            skLineSegment(sketch, "E116", {"start": v(-23.55, 50.56) * mm, "end": v(-25.55, 50.47) * mm});
            skPoint(sketch, "E117.0.end.orphan", {"position": v(-22.8, 50.59) * mm});
            skArc(sketch, "E118.0", {"start": v(-12.36, 30.67) * mm, "mid": v(-19.37, 39.27) * mm, "end": v(-22.72, 49.85) * mm});
            skArc(sketch, "E119.0", {"start": v(-23.55, 50.56) * mm, "mid": v(-23, 50.37) * mm, "end": v(-22.72, 49.85) * mm});
            skSolve(sketch);
        }
        {
            var Q0;
            Q0 = qSketchRegion(id + "F18", true);
            var Q1;
            Q1=makeQuery(id+"F9.opExtrude","CAP_FACE",FACE,{"disambiguationData":[OSD([sQuery(id+"F8.wireOp",EDGE,"E72.0"),sQuery(id+"F8.wireOp",EDGE,"E73.0"),sQuery(id+"F8.wireOp",EDGE,"E74.0"),sQuery(id+"F8.wireOp",EDGE,"E75.0"),sQuery(id+"F8.wireOp",EDGE,"E76.0"),sQuery(id+"F8.wireOp",EDGE,"E77.0"),sQuery(id+"F8.wireOp",EDGE,"E78.0"),sQuery(id+"F8.wireOp",EDGE,"E79.0"),sQuery(id+"F8.wireOp",EDGE,"E80.0"),sQuery(id+"F8.wireOp",EDGE,"E81.0"),sQuery(id+"F8.wireOp",EDGE,"E82.0"),sQuery(id+"F8.wireOp",EDGE,"E83.0"),sQuery(id+"F8.wireOp",EDGE,"E84.0"),sQuery(id+"F8.wireOp",EDGE,"E85.0"),sQuery(id+"F8.wireOp",EDGE,"E86.0"),sQuery(id+"F8.wireOp",EDGE,"E87.0")])],"isStart":true});
            extrude(context, id + "F19", {"entities" : qUnion([Q0]), "operationType" : NewBodyOperationType.ADD, "endBound" : BoundingType.UP_TO_SURFACE, "oppositeDirection" : true, "endBoundEntityFace" : qUnion([Q1]), "depth" : 25 * mm});
        }
        {
            var Q0;
            {var subQ0=makeQuery(id+"F1.opExtrude","CAP_FACE",FACE,{"disambiguationData":[OSD([sQuery(id+"F0.wireOp",EDGE,"E0")])],"isStart":false});var subQ1=makeQuery(id+"F11.opPattern","COPY",FACE,{"derivedFrom":subQ0,"instanceName":"1"});Q0=makeQuery(id+"F17.boolean.opBoolean","MERGE",FACE,{"derivedFrom":[makeQuery(id+"F15.opBoolean","MERGE",FACE,{"derivedFrom":[subQ0,makeQuery(id+"F10.opPattern","COPY",FACE,{"derivedFrom":subQ0,"instanceName":"1"}),subQ1,makeQuery(id+"F14.opPattern","COPY",FACE,{"derivedFrom":subQ1,"instanceName":"1"})]}),makeQuery(id+"F17.opExtrude","CAP_FACE",FACE,{"disambiguationData":[OSD([sQuery(id+"F16.wireOp",EDGE,"E88.0"),sQuery(id+"F16.wireOp",EDGE,"E89.0"),sQuery(id+"F16.wireOp",EDGE,"E90.0"),sQuery(id+"F16.wireOp",EDGE,"E91.0")])],"isStart":true}),makeQuery(id+"F17.opExtrude","CAP_FACE",FACE,{"disambiguationData":[OSD([sQuery(id+"F16.wireOp",EDGE,"E92.0"),sQuery(id+"F16.wireOp",EDGE,"E93.0"),sQuery(id+"F16.wireOp",EDGE,"E94.0"),sQuery(id+"F16.wireOp",EDGE,"E95.0")])],"isStart":true}),makeQuery(id+"F17.opExtrude","CAP_FACE",FACE,{"disambiguationData":[OSD([sQuery(id+"F16.wireOp",EDGE,"E96.0"),sQuery(id+"F16.wireOp",EDGE,"E97.0"),sQuery(id+"F16.wireOp",EDGE,"E98.0"),sQuery(id+"F16.wireOp",EDGE,"E99.0")])],"isStart":true}),makeQuery(id+"F17.opExtrude","CAP_FACE",FACE,{"disambiguationData":[OSD([sQuery(id+"F16.wireOp",EDGE,"E100.0"),sQuery(id+"F16.wireOp",EDGE,"E101.0"),sQuery(id+"F16.wireOp",EDGE,"E102.0"),sQuery(id+"F16.wireOp",EDGE,"E103.0")])],"isStart":true}),makeQuery(id+"F17.opExtrude","CAP_FACE",FACE,{"disambiguationData":[OSD([sQuery(id+"F16.wireOp",EDGE,"E104.0"),sQuery(id+"F16.wireOp",EDGE,"E106.0"),sQuery(id+"F16.wireOp",EDGE,"E107.0"),sQuery(id+"F16.wireOp",EDGE,"E108.0")])],"isStart":true}),makeQuery(id+"F17.opExtrude","CAP_FACE",FACE,{"disambiguationData":[OSD([sQuery(id+"F16.wireOp",EDGE,"E109.0"),sQuery(id+"F16.wireOp",EDGE,"E110.0"),sQuery(id+"F16.wireOp",EDGE,"E111.0"),sQuery(id+"F16.wireOp",EDGE,"E112.0")])],"isStart":true})]});}
            var sketch = newSketch(context, id + "F20", { "sketchPlane" : qUnion([Q0])});
            skArc(sketch, "E120", {"start": v(-10.4, 50.87) * mm, "mid": v(-3.1, 51.64) * mm, "end": v(-6.2, 58.28) * mm});
            skFitSpline(sketch, "E121.0", {"points": [v(-15.75, 57.6) * mm, v(-15.4, 58.44) * mm, v(-14.44, 59.99) * mm, v(-12.47, 61.79) * mm, v(-10.07, 62.98) * mm, v(-8.3, 63.31) * mm, v(-7.37, 63.35) * mm]});
            skFitSpline(sketch, "E121.1", {"points": [v(-14.14, 47.56) * mm, v(-14.75, 48.25) * mm, v(-15.74, 49.77) * mm, v(-16.52, 52.33) * mm, v(-16.58, 55) * mm, v(-16.11, 56.75) * mm, v(-15.75, 57.6) * mm]});
            skLineSegment(sketch, "E121.2", {"start": v(-13.22, 51.05) * mm, "end": v(-14.52, 49.9) * mm});
            skLineSegment(sketch, "E122", {"start": v(-7.56, 62.3) * mm, "end": v(-8.1, 59.44) * mm});
            skLineSegment(sketch, "E123", {"start": v(-13.22, 51.05) * mm, "end": v(-12.32, 51.84) * mm});
            skLineSegment(sketch, "E124", {"start": v(60.2, 58.28) * mm, "end": v(60.2, 58.28) * mm});
            skPoint(sketch, "E125.0", {"position": v(52.66, 47.92) * mm});
            skPoint(sketch, "E126.0", {"position": v(61, 62.67) * mm});
            skArc(sketch, "E127", {"start": v(56, 50.87) * mm, "mid": v(63.3, 51.65) * mm, "end": v(60.17, 58.28) * mm});
            skArc(sketch, "E128", {"start": v(58, 63.25) * mm, "mid": v(51.11, 58.53) * mm, "end": v(50.61, 50.19) * mm});
            skLineSegment(sketch, "E129.0", {"start": v(58.9, 62.32) * mm, "end": v(58.38, 59.43) * mm});
            skLineSegment(sketch, "E130.0", {"start": v(54.08, 51.84) * mm, "end": v(51.88, 49.9) * mm});
            skArc(sketch, "E131", {"start": v(-4.4, -1.9) * mm, "mid": v(2.29, -4.89) * mm, "end": v(2.92, 2.41) * mm});
            skArc(sketch, "E132", {"start": v(3.51, 7.82) * mm, "mid": v(-4.82, 7.18) * mm, "end": v(-9.42, 0.2) * mm});
            skLineSegment(sketch, "E133.0", {"start": v(-5.6, -0.1) * mm, "end": v(-8.47, -0.69) * mm});
            skLineSegment(sketch, "E134.0", {"start": v(3.83, 6.55) * mm, "end": v(1.92, 4.32) * mm});
            skPoint(sketch, "E135.orphan", {"position": v(71.68, 0) * mm});
            skArc(sketch, "E136", {"start": v(62.3, -1.9) * mm, "mid": v(68.99, -4.89) * mm, "end": v(69.62, 2.41) * mm});
            skArc(sketch, "E137", {"start": v(70.21, 7.82) * mm, "mid": v(61.88, 7.18) * mm, "end": v(57.28, 0.2) * mm});
            skLineSegment(sketch, "E138.0", {"start": v(61.1, -0.1) * mm, "end": v(58.23, -0.69) * mm});
            skLineSegment(sketch, "E139.0", {"start": v(70.53, 6.55) * mm, "end": v(68.62, 4.32) * mm});
            skLineSegment(sketch, "E140", {"start": v(62.3, -1.9) * mm, "end": v(62.05, -0.73) * mm});
            skLineSegment(sketch, "E141", {"start": v(69.62, 2.41) * mm, "end": v(68.7, 3.2) * mm});
            skLineSegment(sketch, "E142", {"start": v(-4.4, -1.9) * mm, "end": v(-4.65, -0.73) * mm});
            skLineSegment(sketch, "E143", {"start": v(2.92, 2.41) * mm, "end": v(2, 3.2) * mm});
            skLineSegment(sketch, "E144", {"start": v(-10.4, 50.87) * mm, "end": v(-11.19, 51.77) * mm});
            skLineSegment(sketch, "E145", {"start": v(-6.2, 58.28) * mm, "end": v(-7.45, 58.51) * mm});
            skLineSegment(sketch, "E146", {"start": v(56, 50.87) * mm, "end": v(55.21, 51.77) * mm});
            skLineSegment(sketch, "E147", {"start": v(60.17, 58.28) * mm, "end": v(59.02, 58.5) * mm});
            skPoint(sketch, "E148.visualSharp", {"position": v(-8.24, 58.66) * mm});
            skArc(sketch, "E148.filletArc", {"start": v(-8.1, 59.44) * mm, "mid": v(-7.97, 58.84) * mm, "end": v(-7.45, 58.51) * mm});
            skPoint(sketch, "E149.visualSharp", {"position": v(-7.37, 63.35) * mm});
            skArc(sketch, "E149.filletArc", {"start": v(-7.56, 62.3) * mm, "mid": v(-7.78, 63) * mm, "end": v(-8.47, 63.24) * mm});
            skPoint(sketch, "E150.visualSharp", {"position": v(-15.3, 49.2) * mm});
            skArc(sketch, "E150.filletArc", {"start": v(-15.79, 50.19) * mm, "mid": v(-15.23, 49.72) * mm, "end": v(-14.52, 49.9) * mm});
            skPoint(sketch, "E151.visualSharp", {"position": v(-11.72, 52.37) * mm});
            skArc(sketch, "E151.filletArc", {"start": v(-11.19, 51.77) * mm, "mid": v(-11.74, 52.04) * mm, "end": v(-12.32, 51.84) * mm});
            skPoint(sketch, "E152.visualSharp", {"position": v(51.1, 49.2) * mm});
            skArc(sketch, "E152.filletArc", {"start": v(50.61, 50.19) * mm, "mid": v(51.17, 49.72) * mm, "end": v(51.88, 49.9) * mm});
            skPoint(sketch, "E153.visualSharp", {"position": v(54.68, 52.37) * mm});
            skArc(sketch, "E153.filletArc", {"start": v(55.21, 51.77) * mm, "mid": v(54.66, 52.04) * mm, "end": v(54.08, 51.84) * mm});
            skPoint(sketch, "E154.visualSharp", {"position": v(58.23, 58.64) * mm});
            skArc(sketch, "E154.filletArc", {"start": v(58.38, 59.43) * mm, "mid": v(58.5, 58.83) * mm, "end": v(59.02, 58.5) * mm});
            skPoint(sketch, "E155.visualSharp", {"position": v(59.1, 63.35) * mm});
            skArc(sketch, "E155.filletArc", {"start": v(58.9, 62.32) * mm, "mid": v(58.7, 63.02) * mm, "end": v(58, 63.25) * mm});
            skPoint(sketch, "E156.visualSharp", {"position": v(-4.8, 0.06) * mm});
            skArc(sketch, "E156.filletArc", {"start": v(-4.65, -0.73) * mm, "mid": v(-4.99, -0.22) * mm, "end": v(-5.6, -0.1) * mm});
            skPoint(sketch, "E157.visualSharp", {"position": v(-9.5, -0.9) * mm});
            skArc(sketch, "E157.filletArc", {"start": v(-9.42, 0.2) * mm, "mid": v(-9.17, -0.49) * mm, "end": v(-8.47, -0.69) * mm});
            skPoint(sketch, "E158.visualSharp", {"position": v(1.4, 3.71) * mm});
            skArc(sketch, "E158.filletArc", {"start": v(1.92, 4.32) * mm, "mid": v(1.73, 3.74) * mm, "end": v(2, 3.2) * mm});
            skPoint(sketch, "E159.visualSharp", {"position": v(4.5, 7.35) * mm});
            skArc(sketch, "E159.filletArc", {"start": v(3.83, 6.55) * mm, "mid": v(4, 7.27) * mm, "end": v(3.51, 7.82) * mm});
            skPoint(sketch, "E160.visualSharp", {"position": v(57.2, -0.9) * mm});
            skArc(sketch, "E160.filletArc", {"start": v(57.28, 0.2) * mm, "mid": v(57.53, -0.49) * mm, "end": v(58.23, -0.69) * mm});
            skPoint(sketch, "E161.visualSharp", {"position": v(71.2, 7.35) * mm});
            skArc(sketch, "E161.filletArc", {"start": v(70.53, 6.55) * mm, "mid": v(70.7, 7.27) * mm, "end": v(70.21, 7.82) * mm});
            skPoint(sketch, "E162.visualSharp", {"position": v(68.1, 3.71) * mm});
            skArc(sketch, "E162.filletArc", {"start": v(68.62, 4.32) * mm, "mid": v(68.43, 3.74) * mm, "end": v(68.7, 3.2) * mm});
            skPoint(sketch, "E163.visualSharp", {"position": v(61.9, 0.06) * mm});
            skArc(sketch, "E163.filletArc", {"start": v(62.05, -0.73) * mm, "mid": v(61.71, -0.22) * mm, "end": v(61.1, -0.1) * mm});
            skSolve(sketch);
        }
        {
            var Q0;
            Q0 = qSketchRegion(id + "F20", true);
            var Q1;
            Q1=makeQuery(id+"F14.opPattern","COPY",FACE,{"derivedFrom":makeQuery(id+"F11.opPattern","COPY",FACE,{"derivedFrom":makeQuery(id+"F9.opExtrude","CAP_FACE",FACE,{"disambiguationData":[OSD([sQuery(id+"F8.wireOp",EDGE,"E72.0"),sQuery(id+"F8.wireOp",EDGE,"E73.0"),sQuery(id+"F8.wireOp",EDGE,"E74.0"),sQuery(id+"F8.wireOp",EDGE,"E75.0"),sQuery(id+"F8.wireOp",EDGE,"E76.0"),sQuery(id+"F8.wireOp",EDGE,"E77.0"),sQuery(id+"F8.wireOp",EDGE,"E78.0"),sQuery(id+"F8.wireOp",EDGE,"E79.0"),sQuery(id+"F8.wireOp",EDGE,"E80.0"),sQuery(id+"F8.wireOp",EDGE,"E81.0"),sQuery(id+"F8.wireOp",EDGE,"E82.0"),sQuery(id+"F8.wireOp",EDGE,"E83.0"),sQuery(id+"F8.wireOp",EDGE,"E84.0"),sQuery(id+"F8.wireOp",EDGE,"E85.0"),sQuery(id+"F8.wireOp",EDGE,"E86.0"),sQuery(id+"F8.wireOp",EDGE,"E87.0")])],"isStart":true}),"instanceName":"1"}),"instanceName":"1"});
            extrude(context, id + "F21", {"entities" : qUnion([Q0]), "operationType" : NewBodyOperationType.REMOVE, "endBound" : BoundingType.UP_TO_SURFACE, "oppositeDirection" : true, "endBoundEntityFace" : qUnion([Q1]), "depth" : 25 * mm});
        }
        {
            var Q0;
            {var subQ0=makeQuery(id+"F9.opExtrude","CAP_FACE",FACE,{"disambiguationData":[OSD([sQuery(id+"F8.wireOp",EDGE,"E72.0"),sQuery(id+"F8.wireOp",EDGE,"E73.0"),sQuery(id+"F8.wireOp",EDGE,"E74.0"),sQuery(id+"F8.wireOp",EDGE,"E75.0"),sQuery(id+"F8.wireOp",EDGE,"E76.0"),sQuery(id+"F8.wireOp",EDGE,"E77.0"),sQuery(id+"F8.wireOp",EDGE,"E78.0"),sQuery(id+"F8.wireOp",EDGE,"E79.0"),sQuery(id+"F8.wireOp",EDGE,"E80.0"),sQuery(id+"F8.wireOp",EDGE,"E81.0"),sQuery(id+"F8.wireOp",EDGE,"E82.0"),sQuery(id+"F8.wireOp",EDGE,"E83.0"),sQuery(id+"F8.wireOp",EDGE,"E84.0"),sQuery(id+"F8.wireOp",EDGE,"E85.0"),sQuery(id+"F8.wireOp",EDGE,"E86.0"),sQuery(id+"F8.wireOp",EDGE,"E87.0")])],"isStart":false});var subQ1=makeQuery(id+"F11.opPattern","COPY",FACE,{"derivedFrom":subQ0,"instanceName":"1"});Q0=makeQuery(id+"F19.boolean.opBoolean","MERGE",FACE,{"derivedFrom":[makeQuery(id+"F17.boolean.opBoolean","MERGE",FACE,{"derivedFrom":[makeQuery(id+"F15.opBoolean","MERGE",FACE,{"derivedFrom":[subQ0,makeQuery(id+"F10.opPattern","COPY",FACE,{"derivedFrom":subQ0,"instanceName":"1"}),subQ1,makeQuery(id+"F14.opPattern","COPY",FACE,{"derivedFrom":subQ1,"instanceName":"1"})]}),makeQuery(id+"F17.opExtrude","CAP_FACE",FACE,{"disambiguationData":[OSD([sQuery(id+"F16.wireOp",EDGE,"E88.0"),sQuery(id+"F16.wireOp",EDGE,"E89.0"),sQuery(id+"F16.wireOp",EDGE,"E90.0"),sQuery(id+"F16.wireOp",EDGE,"E91.0")])],"isStart":false}),makeQuery(id+"F17.opExtrude","CAP_FACE",FACE,{"disambiguationData":[OSD([sQuery(id+"F16.wireOp",EDGE,"E92.0"),sQuery(id+"F16.wireOp",EDGE,"E93.0"),sQuery(id+"F16.wireOp",EDGE,"E94.0"),sQuery(id+"F16.wireOp",EDGE,"E95.0")])],"isStart":false}),makeQuery(id+"F17.opExtrude","CAP_FACE",FACE,{"disambiguationData":[OSD([sQuery(id+"F16.wireOp",EDGE,"E96.0"),sQuery(id+"F16.wireOp",EDGE,"E97.0"),sQuery(id+"F16.wireOp",EDGE,"E98.0"),sQuery(id+"F16.wireOp",EDGE,"E99.0")])],"isStart":false}),makeQuery(id+"F17.opExtrude","CAP_FACE",FACE,{"disambiguationData":[OSD([sQuery(id+"F16.wireOp",EDGE,"E100.0"),sQuery(id+"F16.wireOp",EDGE,"E101.0"),sQuery(id+"F16.wireOp",EDGE,"E102.0"),sQuery(id+"F16.wireOp",EDGE,"E103.0")])],"isStart":false}),makeQuery(id+"F17.opExtrude","CAP_FACE",FACE,{"disambiguationData":[OSD([sQuery(id+"F16.wireOp",EDGE,"E104.0"),sQuery(id+"F16.wireOp",EDGE,"E106.0"),sQuery(id+"F16.wireOp",EDGE,"E107.0"),sQuery(id+"F16.wireOp",EDGE,"E108.0")])],"isStart":false}),makeQuery(id+"F17.opExtrude","CAP_FACE",FACE,{"disambiguationData":[OSD([sQuery(id+"F16.wireOp",EDGE,"E109.0"),sQuery(id+"F16.wireOp",EDGE,"E110.0"),sQuery(id+"F16.wireOp",EDGE,"E111.0"),sQuery(id+"F16.wireOp",EDGE,"E112.0")])],"isStart":false})]}),makeQuery(id+"F19.opExtrude","CAP_FACE",FACE,{"disambiguationData":[OSD([sQuery(id+"F18.wireOp",EDGE,"E113.0"),sQuery(id+"F18.wireOp",EDGE,"E114.0"),sQuery(id+"F18.wireOp",EDGE,"E115.0"),sQuery(id+"F18.wireOp",EDGE,"E116"),sQuery(id+"F18.wireOp",EDGE,"E118.0"),sQuery(id+"F18.wireOp",EDGE,"E119.0")])],"isStart":true})]});}
            extrude(context, id + "F22", {"entities" : qUnion([Q0]), "operationType" : NewBodyOperationType.ADD, "depth" : 5 * mm});
        }
        {
            var Q0;
            Q0=makeQuery(id+"F22.opExtrude","CAP_FACE",FACE,{"disambiguationData":[OSD([sQuery(id+"F8.wireOp",EDGE,"6bac64cb-5eda-4021-aea4-5ae1bc615e7b.0.0"),sQuery(id+"F8.wireOp",EDGE,"6bac64cb-5eda-4021-aea4-5ae1bc615e7b.0.1"),sQuery(id+"F8.wireOp",EDGE,"6bac64cb-5eda-4021-aea4-5ae1bc615e7b.0.2"),sQuery(id+"F8.wireOp",EDGE,"6bac64cb-5eda-4021-aea4-5ae1bc615e7b.0.3"),sQuery(id+"F8.wireOp",EDGE,"6bac64cb-5eda-4021-aea4-5ae1bc615e7b.0.4"),sQuery(id+"F8.wireOp",EDGE,"6bac64cb-5eda-4021-aea4-5ae1bc615e7b.0.5"),sQuery(id+"F8.wireOp",EDGE,"6bac64cb-5eda-4021-aea4-5ae1bc615e7b.0.6"),sQuery(id+"F8.wireOp",EDGE,"6bac64cb-5eda-4021-aea4-5ae1bc615e7b.0.7"),sQuery(id+"F18.wireOp",EDGE,"E113.0"),sQuery(id+"F18.wireOp",EDGE,"E117.0"),sQuery(id+"F18.wireOp",EDGE,"E114.0"),sQuery(id+"F18.wireOp",EDGE,"E115.0"),sQuery(id+"F18.wireOp",EDGE,"E116")])],"isStart":false});
            var sketch = newSketch(context, id + "F23", { "sketchPlane" : qUnion([Q0])});
            skLineSegment(sketch, "E164", {"start": v(46.02, 92.84) * mm, "end": v(-105.66, 92.84) * mm});
            skLineSegment(sketch, "E165", {"start": v(-105.66, 92.84) * mm, "end": v(-105.66, -36.23) * mm});
            skLineSegment(sketch, "E166", {"start": v(-105.66, -36.23) * mm, "end": v(46.02, -36.23) * mm});
            skLineSegment(sketch, "E167", {"start": v(46.02, 92.84) * mm, "end": v(46.02, -36.23) * mm});
            skSolve(sketch);
        }
        {
            var Q0;
            Q0 = qSketchRegion(id + "F23", true);
            extrude(context, id + "F24", {"entities" : qUnion([Q0]), "oppositeDirection" : true, "depth" : 12.7 * mm});
        }
        {
            var Q0;
            Q0=makeQuery(id+"F14.opPattern","COPY",BODY,{"derivedFrom":makeQuery(id+"F11.opPattern","COPY",BODY,{"derivedFrom":makeQuery(id+"F1.opExtrude","SWEPT_BODY",BODY,{"disambiguationData":[OSD([sQuery(id+"F0.wireOp",EDGE,"E0")])]}),"instanceName":"1"}),"instanceName":"1"});
            var Q1;
            Q1=makeQuery(id+"F24.opExtrude","SWEPT_BODY",BODY,{"disambiguationData":[OSD([sQuery(id+"F23.wireOp",EDGE,"E164"),sQuery(id+"F23.wireOp",EDGE,"E165"),sQuery(id+"F23.wireOp",EDGE,"E166"),sQuery(id+"F23.wireOp",EDGE,"E167")])]});
            booleanBodies(context, id + "F25", {"operationType" : BooleanOperationType.SUBTRACTION, "tools" : qUnion([Q0]), "targets" : qUnion([Q1])});
        }
        {
            var Q0;
            Q0=makeQuery(id+"F25.opBoolean","COPY",FACE,{"derivedFrom":makeQuery(id+"F19.opExtrude","CAP_FACE",FACE,{"disambiguationData":[OSD([sQuery(id+"F18.wireOp",EDGE,"E113.0"),sQuery(id+"F18.wireOp",EDGE,"E114.0"),sQuery(id+"F18.wireOp",EDGE,"E115.0"),sQuery(id+"F18.wireOp",EDGE,"E116"),sQuery(id+"F18.wireOp",EDGE,"E118.0"),sQuery(id+"F18.wireOp",EDGE,"E119.0")])],"isStart":false})});
            cPlane(context, id + "F26", {"entities" : qUnion([Q0]), "cplaneType" : CPlaneType.OFFSET, "offset" : 3 * mm, "width" : 150 * mm, "height" : 150 * mm});
        }
        {
            var Q0;
            Q0=qCreatedBy(id+"F26.planeOp",FACE);
            var sketch = newSketch(context, id + "F27", { "sketchPlane" : qUnion([Q0])});
            skArc(sketch, "E168.0", {"start": v(-47.5, -24.08) * mm, "mid": v(-70, -31.05) * mm, "end": v(-90.46, -19.35) * mm});
            skLineSegment(sketch, "E169.0", {"start": v(-78.34, -36.23) * mm, "end": v(-55.99, -36.23) * mm});
            skLineSegment(sketch, "E170", {"start": v(-76.16, -29.7) * mm, "end": v(-78.34, -36.23) * mm});
            skLineSegment(sketch, "E171", {"start": v(-57.97, -29.88) * mm, "end": v(-55.99, -36.23) * mm});
            skPoint(sketch, "E172.orphan", {"position": v(-105.66, -36.23) * mm});
            skPoint(sketch, "E173.orphan", {"position": v(46.02, -36.23) * mm});
            skSolve(sketch);
        }
        {
            var Q0;
            Q0 = qSketchRegion(id + "F27", true);
            extrude(context, id + "F28", {"entities" : qUnion([Q0]), "operationType" : NewBodyOperationType.REMOVE, "depth" : 25 * mm});
        }
        {
            var Q0;
            Q0=makeQuery(id+"F24.opExtrude","SWEPT_BODY",BODY,{"disambiguationData":[OSD([sQuery(id+"F23.wireOp",EDGE,"E164"),sQuery(id+"F23.wireOp",EDGE,"E165"),sQuery(id+"F23.wireOp",EDGE,"E166"),sQuery(id+"F23.wireOp",EDGE,"E167")])]});
            var Q1;
            Q1=makeQuery(id+"F24.opExtrude","CAP_EDGE",EDGE,{"disambiguationData":[OSD([sQuery(id+"F23.wireOp",EDGE,"E166")])],"isStart":false});
            transform(context, id + "F29", {"entities" : qUnion([Q0]), "transformType" : TransformType.ROTATION, "transformAxis" : qUnion([Q1]), "angle" : 90 * degree, "oppositeDirection" : true, "makeCopy" : false});
        }
        {
            var Q0;
            Q0=makeQuery(id+"F24.opExtrude","SWEPT_BODY",BODY,{"disambiguationData":[OSD([sQuery(id+"F23.wireOp",EDGE,"E164"),sQuery(id+"F23.wireOp",EDGE,"E165"),sQuery(id+"F23.wireOp",EDGE,"E166"),sQuery(id+"F23.wireOp",EDGE,"E167")])]});
            transform(context, id + "F30", {"entities" : qUnion([Q0]), "transformType" : TransformType.TRANSLATION_3D, "dx" : -29.82 * mm, "dy" : 71.34 * mm, "dz" : 36.23 * mm, "makeCopy" : false});
        }
    });
